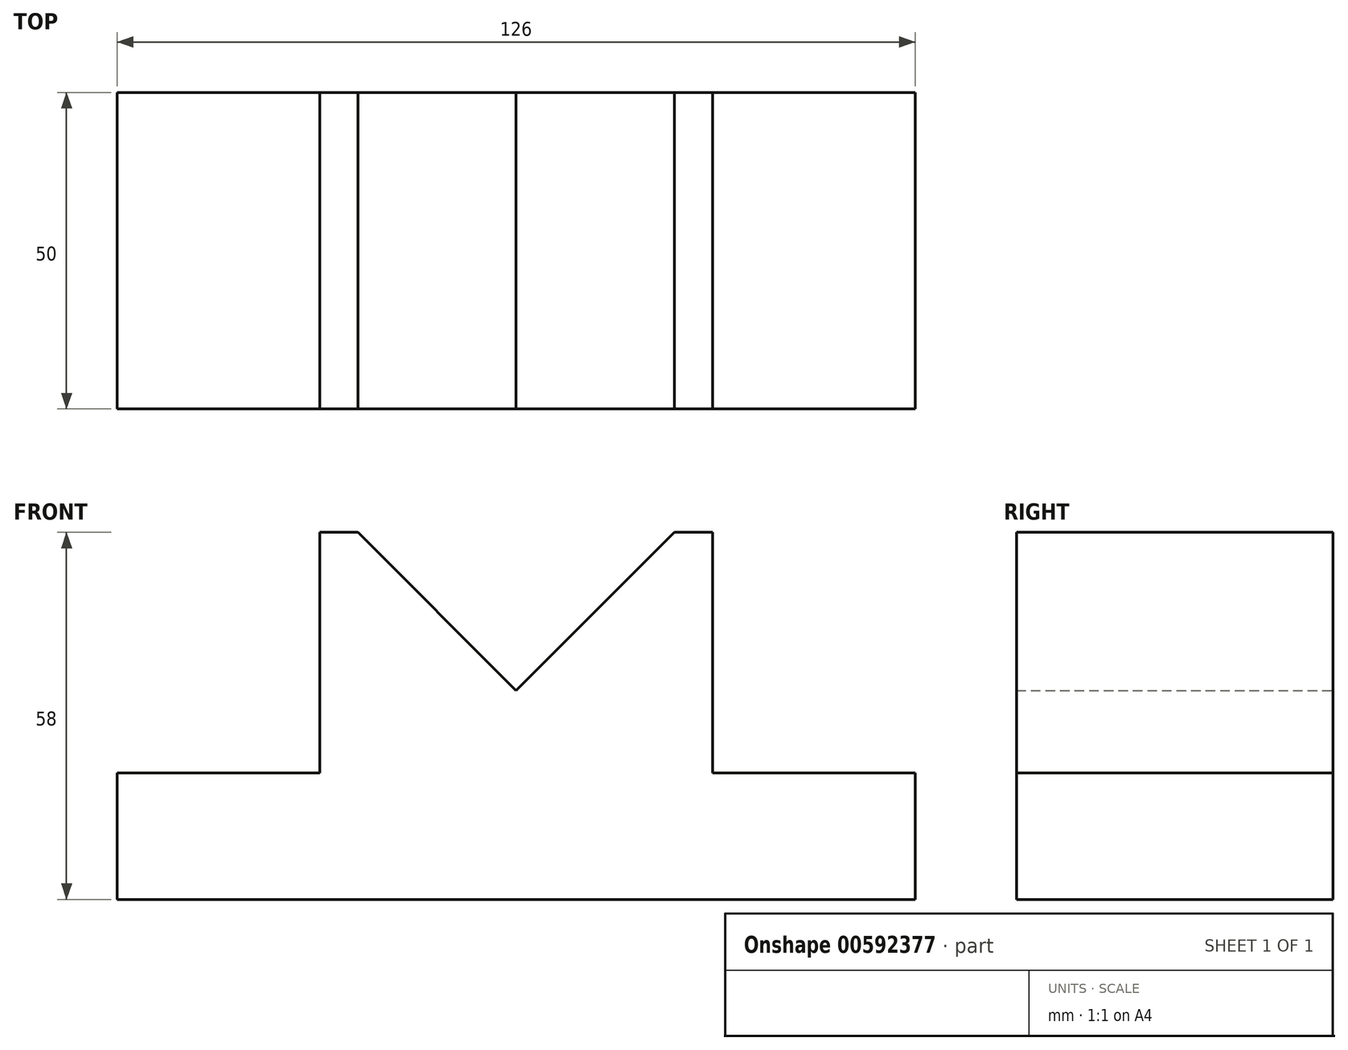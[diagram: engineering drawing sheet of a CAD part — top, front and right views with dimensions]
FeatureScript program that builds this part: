
annotation { "Feature Type Name" : "Feature", "Feature Type Description" : "" }
export const myFeature = defineFeature(function(context is Context, id is Id, definition is map)
    precondition{}
    {
        {
            var Q0;
            Q0=qCreatedBy(makeId("Front.planeOp"),FACE);
            var sketch = newSketch(context, id + "F0", { "sketchPlane" : qUnion([Q0])});
            skLineSegment(sketch, "E0", {"start": v(-63, 8.55) * mm, "end": v(63, 8.55) * mm});
            skLineSegment(sketch, "E1", {"start": v(63, 8.55) * mm, "end": v(63, 28.55) * mm});
            skLineSegment(sketch, "E2", {"start": v(63, 28.55) * mm, "end": v(31, 28.55) * mm});
            skLineSegment(sketch, "E3", {"start": v(31, 28.55) * mm, "end": v(31, 66.55) * mm});
            skLineSegment(sketch, "E4", {"start": v(31, 66.55) * mm, "end": v(25, 66.55) * mm});
            skLineSegment(sketch, "E5", {"start": v(25, 66.55) * mm, "end": v(0, 41.55) * mm});
            skLineSegment(sketch, "E6", {"start": v(0, 41.55) * mm, "end": v(-25, 66.55) * mm});
            skLineSegment(sketch, "E7", {"start": v(-25, 66.55) * mm, "end": v(-31, 66.55) * mm});
            skLineSegment(sketch, "E8", {"start": v(-31, 66.55) * mm, "end": v(-31, 28.55) * mm});
            skLineSegment(sketch, "E9", {"start": v(-31, 28.55) * mm, "end": v(-63, 28.55) * mm});
            skLineSegment(sketch, "E10", {"start": v(-63, 28.55) * mm, "end": v(-63, 8.55) * mm});
            skSolve(sketch);
        }
        {
            var Q0;
            Q0=makeQuery(id+"F0.imprint","IMPRINT",FACE,{"disambiguationData":[TD([[makeQuery(id+"F0.imprint","IMPRINT",EDGE,{"derivedFrom":sQuery(id+"F0.wireOp",EDGE,"E0")}),1.0]])]});
            extrude(context, id + "F1", {"entities" : qUnion([Q0]), "endBound" : BoundingType.SYMMETRIC, "depth" : 50 * mm, "offsetDistance" : 25 * mm});
        }
    });
